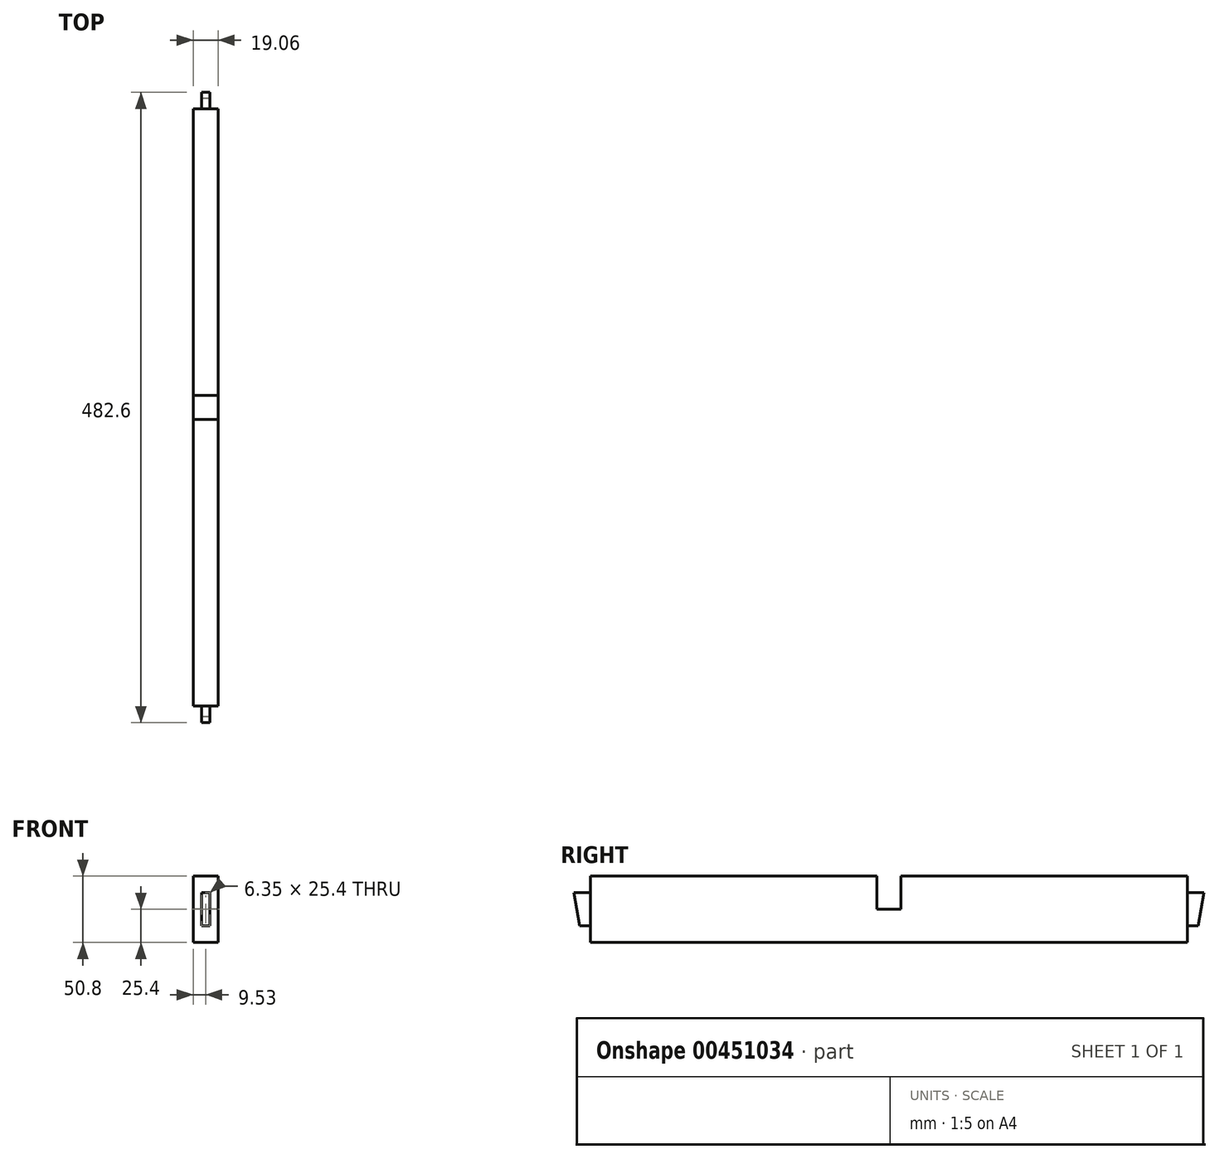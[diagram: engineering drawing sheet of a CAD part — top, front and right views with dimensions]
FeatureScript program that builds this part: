
annotation { "Feature Type Name" : "Feature", "Feature Type Description" : "" }
export const myFeature = defineFeature(function(context is Context, id is Id, definition is map)
    precondition{}
    {
        {
            var Q0;
            Q0=qCreatedBy(makeId("Right.planeOp"),FACE);
            var sketch = newSketch(context, id + "F0", { "sketchPlane" : qUnion([Q0])});
            skLineSegment(sketch, "E0.bottom", {"start": v(-228.6, 25.4) * mm, "end": v(228.6, 25.4) * mm});
            skLineSegment(sketch, "E0.top", {"start": v(-228.6, -25.4) * mm, "end": v(228.6, -25.4) * mm});
            skLineSegment(sketch, "E0.left", {"start": v(-228.6, 25.4) * mm, "end": v(-228.6, -25.4) * mm});
            skLineSegment(sketch, "E0.right", {"start": v(228.6, 25.4) * mm, "end": v(228.6, -25.4) * mm});
            skPoint(sketch, "E0.middle", {"position": v(0, 0) * mm});
            skSolve(sketch);
        }
        {
            var Q0;
            Q0=makeQuery(id+"F0.imprint","IMPRINT",FACE,{"disambiguationData":[TD([[makeQuery(id+"F0.imprint","IMPRINT",EDGE,{"derivedFrom":sQuery(id+"F0.wireOp",EDGE,"E0.bottom")}),-1.0]])]});
            extrude(context, id + "F1", {"entities" : qUnion([Q0]), "endBound" : BoundingType.SYMMETRIC, "depth" : 19.05 * mm});
        }
        {
            var Q0;
            Q0=makeQuery(id+"F1.opExtrude","SWEPT_FACE",FACE,{"disambiguationData":[OSD([sQuery(id+"F0.wireOp",EDGE,"E0.bottom")])]});
            var sketch = newSketch(context, id + "F2", { "sketchPlane" : qUnion([Q0])});
            skLineSegment(sketch, "E1.bottom", {"start": v(9.53, 9.24) * mm, "end": v(-9.53, 9.24) * mm});
            skLineSegment(sketch, "E1.top", {"start": v(9.53, -9.24) * mm, "end": v(-9.53, -9.24) * mm});
            skLineSegment(sketch, "E1.left", {"start": v(9.53, 9.24) * mm, "end": v(9.53, -9.24) * mm});
            skLineSegment(sketch, "E1.right", {"start": v(-9.53, 9.24) * mm, "end": v(-9.53, -9.24) * mm});
            skPoint(sketch, "E1.middle", {"position": v(0, 0) * mm});
            skSolve(sketch);
        }
        {
            var Q0;
            Q0=makeQuery(id+"F2.imprint","IMPRINT",FACE,{"disambiguationData":[TD([[makeQuery(id+"F2.imprint","IMPRINT",EDGE,{"derivedFrom":sQuery(id+"F2.wireOp",EDGE,"E1.bottom")}),1.0]])]});
            extrude(context, id + "F3", {"entities" : qUnion([Q0]), "operationType" : NewBodyOperationType.REMOVE, "endBound" : BoundingType.SYMMETRIC, "oppositeDirection" : true, "depth" : 50.8 * mm});
        }
        {
            var Q0;
            Q0=makeQuery(id+"F1.opExtrude","SWEPT_FACE",FACE,{"disambiguationData":[OSD([sQuery(id+"F0.wireOp",EDGE,"E0.left")])]});
            var sketch = newSketch(context, id + "F4", { "sketchPlane" : qUnion([Q0])});
            skLineSegment(sketch, "E2.bottom", {"start": v(-3.17, 12.7) * mm, "end": v(3.18, 12.7) * mm});
            skLineSegment(sketch, "E2.top", {"start": v(-3.18, -12.7) * mm, "end": v(3.17, -12.7) * mm});
            skLineSegment(sketch, "E2.left", {"start": v(-3.17, 12.7) * mm, "end": v(-3.18, -12.7) * mm});
            skLineSegment(sketch, "E2.right", {"start": v(3.18, 12.7) * mm, "end": v(3.17, -12.7) * mm});
            skPoint(sketch, "E2.middle", {"position": v(0, 0) * mm});
            skSolve(sketch);
        }
        {
            var Q0;
            Q0=makeQuery(id+"F4.imprint","IMPRINT",FACE,{"disambiguationData":[TD([[makeQuery(id+"F4.imprint","IMPRINT",EDGE,{"derivedFrom":sQuery(id+"F4.wireOp",EDGE,"E2.bottom")}),-1.0]])]});
            extrude(context, id + "F5", {"entities" : qUnion([Q0]), "operationType" : NewBodyOperationType.ADD, "endBound" : BoundingType.SYMMETRIC, "depth" : 25.4 * mm});
        }
        {
            var Q0;
            Q0=makeQuery(id+"F1.opExtrude","SWEPT_FACE",FACE,{"disambiguationData":[OSD([sQuery(id+"F0.wireOp",EDGE,"E0.right")])]});
            var sketch = newSketch(context, id + "F6", { "sketchPlane" : qUnion([Q0])});
            skLineSegment(sketch, "E3.bottom", {"start": v(-3.17, 12.7) * mm, "end": v(3.18, 12.7) * mm});
            skLineSegment(sketch, "E3.top", {"start": v(-3.18, -12.7) * mm, "end": v(3.17, -12.7) * mm});
            skLineSegment(sketch, "E3.left", {"start": v(-3.17, 12.7) * mm, "end": v(-3.18, -12.7) * mm});
            skLineSegment(sketch, "E3.right", {"start": v(3.18, 12.7) * mm, "end": v(3.17, -12.7) * mm});
            skPoint(sketch, "E3.middle", {"position": v(0, 0) * mm});
            skSolve(sketch);
        }
        {
            var Q0;
            Q0=makeQuery(id+"F6.imprint","IMPRINT",FACE,{"disambiguationData":[TD([[makeQuery(id+"F6.imprint","IMPRINT",EDGE,{"derivedFrom":sQuery(id+"F6.wireOp",EDGE,"E3.bottom")}),-1.0]])]});
            extrude(context, id + "F7", {"entities" : qUnion([Q0]), "operationType" : NewBodyOperationType.ADD, "endBound" : BoundingType.SYMMETRIC, "depth" : 25.4 * mm});
        }
        {
            var Q0;
            Q0=makeQuery(id+"F7.opExtrude","CAP_EDGE",EDGE,{"disambiguationData":[OSD([sQuery(id+"F6.wireOp",EDGE,"E3.top")])],"isStart":false});
            chamfer(context, id + "F8", {"entities" : qUnion([Q0]), "chamferType" : ChamferType.OFFSET_ANGLE, "width" : 25.4 * mm, "oppositeDirection" : false, "angle" : 10 * degree, "tangentPropagation" : true});
        }
        {
            var Q0;
            Q0=makeQuery(id+"F5.opExtrude","CAP_EDGE",EDGE,{"disambiguationData":[OSD([sQuery(id+"F4.wireOp",EDGE,"E2.top")])],"isStart":false});
            chamfer(context, id + "F9", {"entities" : qUnion([Q0]), "chamferType" : ChamferType.OFFSET_ANGLE, "width" : 25.4 * mm, "oppositeDirection" : false, "angle" : 10 * degree, "tangentPropagation" : true});
        }
    });
